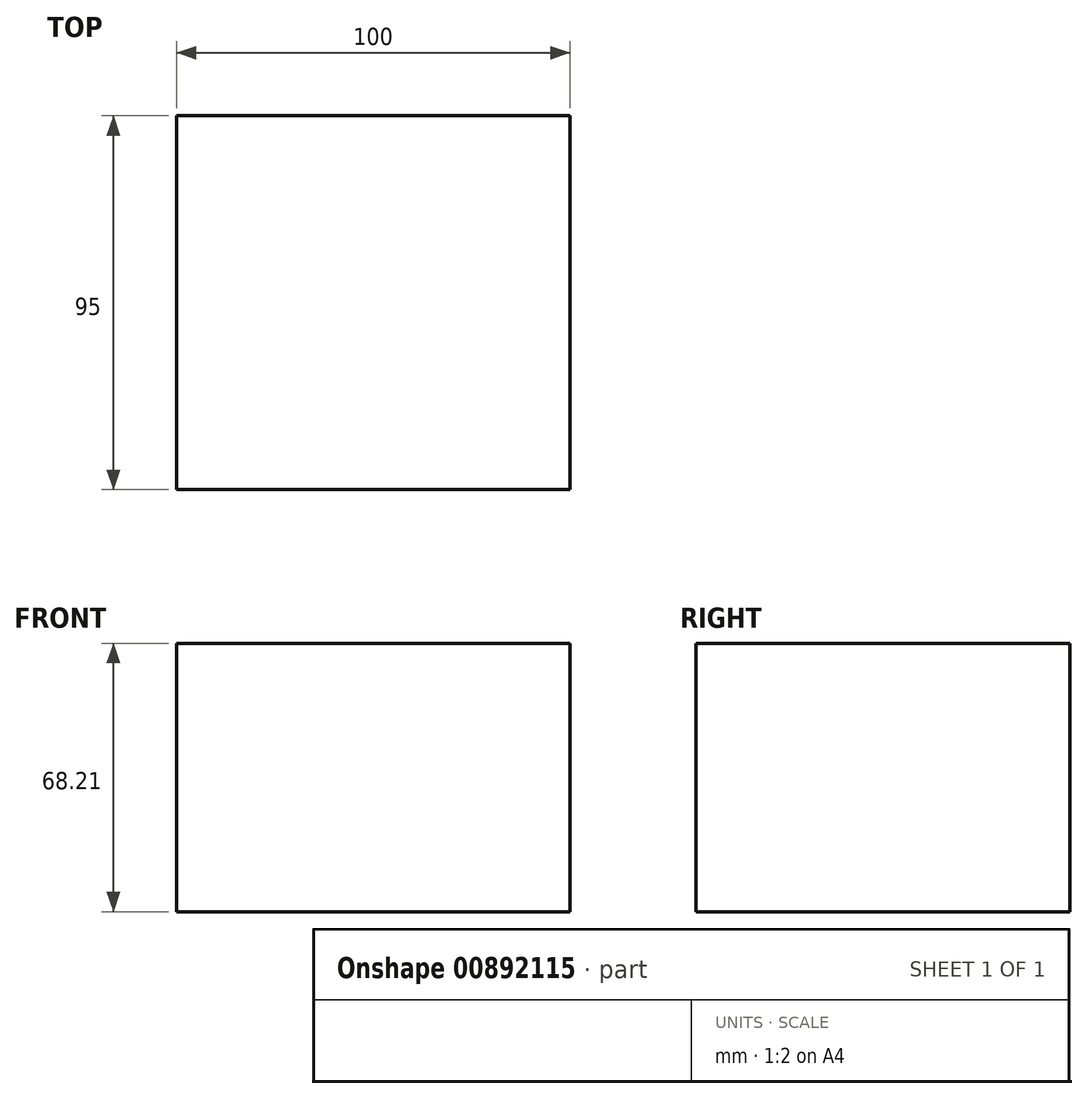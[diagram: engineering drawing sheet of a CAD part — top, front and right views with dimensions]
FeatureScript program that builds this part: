
annotation { "Feature Type Name" : "Feature", "Feature Type Description" : "" }
export const myFeature = defineFeature(function(context is Context, id is Id, definition is map)
    precondition{}
    {
        {
            var Q0;
            Q0=qCreatedBy(makeId("Front.planeOp"),FACE);
            var sketch = newSketch(context, id + "F0", { "sketchPlane" : qUnion([Q0])});
            skLineSegment(sketch, "E0", {"start": v(-49.72, 35.8) * mm, "end": v(50.28, 35.8) * mm});
            skLineSegment(sketch, "E1", {"start": v(50.28, 35.8) * mm, "end": v(50.28, -32.42) * mm});
            skLineSegment(sketch, "E2", {"start": v(50.28, -32.42) * mm, "end": v(-49.72, -32.42) * mm});
            skLineSegment(sketch, "E3", {"start": v(-49.72, -32.42) * mm, "end": v(-49.72, 35.8) * mm});
            skSolve(sketch);
        }
        {
            var Q0;
            Q0=makeQuery(id+"F0.imprint","IMPRINT",FACE,{"disambiguationData":[TD([[makeQuery(id+"F0.imprint","IMPRINT",EDGE,{"derivedFrom":sQuery(id+"F0.wireOp",EDGE,"E0")}),-1.0]])]});
            extrude(context, id + "F1", {"entities" : qUnion([Q0]), "depth" : 95 * mm, "offsetDistance" : 25 * mm});
        }
    });
